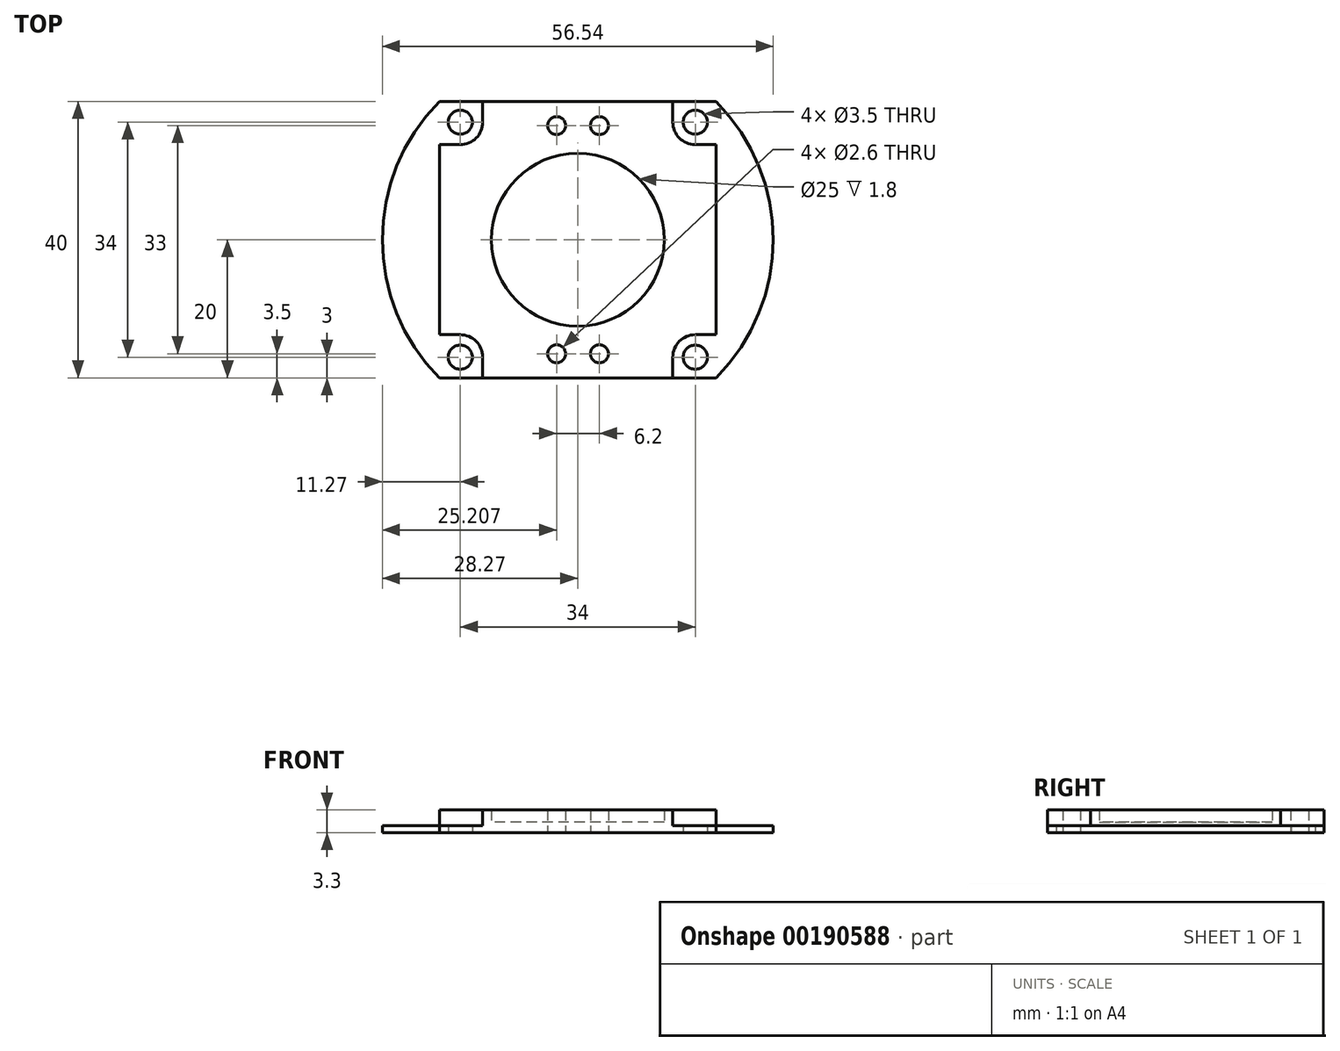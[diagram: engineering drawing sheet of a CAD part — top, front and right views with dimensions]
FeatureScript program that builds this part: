
annotation { "Feature Type Name" : "Feature", "Feature Type Description" : "" }
export const myFeature = defineFeature(function(context is Context, id is Id, definition is map)
    precondition{}
    {
        {
            var Q0;
            Q0=qCreatedBy(makeId("Top.planeOp"),FACE);
            var sketch = newSketch(context, id + "F0", { "sketchPlane" : qUnion([Q0])});
            skLineSegment(sketch, "E0.bottom", {"start": v(20, -20) * mm, "end": v(-20, -20) * mm});
            skLineSegment(sketch, "E0.top", {"start": v(20, 20) * mm, "end": v(-20, 20) * mm});
            skLineSegment(sketch, "E0.left", {"start": v(20, -20) * mm, "end": v(20, 20) * mm});
            skLineSegment(sketch, "E0.right", {"start": v(-20, -20) * mm, "end": v(-20, 20) * mm});
            skPoint(sketch, "E0.middle", {"position": v(0, 0) * mm});
            skArc(sketch, "E1", {"start": v(-20, 20) * mm, "mid": v(-28.27, 0) * mm, "end": v(-20, -20) * mm});
            skArc(sketch, "E2", {"start": v(20, -20) * mm, "mid": v(28.27, 0) * mm, "end": v(20, 20) * mm});
            skLineSegment(sketch, "E3.bottom", {"start": v(13.75, -13.75) * mm, "end": v(-13.75, -13.75) * mm, "construction": true});
            skLineSegment(sketch, "E3.top", {"start": v(13.75, 13.75) * mm, "end": v(-13.75, 13.75) * mm, "construction": true});
            skLineSegment(sketch, "E3.left", {"start": v(13.75, -13.75) * mm, "end": v(13.75, 13.75) * mm, "construction": true});
            skLineSegment(sketch, "E3.right", {"start": v(-13.75, -13.75) * mm, "end": v(-13.75, 13.75) * mm, "construction": true});
            skLineSegment(sketch, "E4", {"start": v(-13.75, 17) * mm, "end": v(-13.75, 20) * mm});
            skLineSegment(sketch, "E5", {"start": v(-17, 13.75) * mm, "end": v(-20, 13.75) * mm});
            skLineSegment(sketch, "E6", {"start": v(13.75, 17) * mm, "end": v(13.75, 20) * mm});
            skLineSegment(sketch, "E7", {"start": v(17, 13.75) * mm, "end": v(20, 13.75) * mm});
            skLineSegment(sketch, "E8", {"start": v(17, -13.75) * mm, "end": v(20, -13.75) * mm});
            skLineSegment(sketch, "E9", {"start": v(13.75, -17) * mm, "end": v(13.75, -20) * mm});
            skLineSegment(sketch, "E10", {"start": v(-13.75, -20) * mm, "end": v(-13.75, -17) * mm});
            skPoint(sketch, "E11.visualSharp", {"position": v(-13.75, 13.75) * mm});
            skArc(sketch, "E11.filletArc", {"start": v(-17, 13.75) * mm, "mid": v(-14.7, 14.7) * mm, "end": v(-13.75, 17) * mm});
            skPoint(sketch, "E12.visualSharp", {"position": v(13.75, 13.75) * mm});
            skArc(sketch, "E12.filletArc", {"start": v(13.75, 17) * mm, "mid": v(14.7, 14.7) * mm, "end": v(17, 13.75) * mm});
            skPoint(sketch, "E13.visualSharp", {"position": v(13.75, -13.75) * mm});
            skArc(sketch, "E13.filletArc", {"start": v(17, -13.75) * mm, "mid": v(14.7, -14.7) * mm, "end": v(13.75, -17) * mm});
            skLineSegment(sketch, "E14", {"start": v(-17, -13.75) * mm, "end": v(-20, -13.75) * mm});
            skPoint(sketch, "E15.visualSharp", {"position": v(-13.75, -13.75) * mm});
            skArc(sketch, "E15.filletArc", {"start": v(-13.75, -17) * mm, "mid": v(-14.7, -14.7) * mm, "end": v(-17, -13.75) * mm});
            skLineSegment(sketch, "E16", {"start": v(0.04, 24.78) * mm, "end": v(0.04, -24.04) * mm, "construction": true});
            skLineSegment(sketch, "E17", {"start": v(-35.36, 0) * mm, "end": v(34.45, 0) * mm, "construction": true});
            skPoint(sketch, "E18", {"position": v(-3.06, 16.5) * mm});
            skPoint(sketch, "E19", {"position": v(3.14, 16.5) * mm});
            skPoint(sketch, "E20", {"position": v(-3.06, -16.5) * mm});
            skPoint(sketch, "E21", {"position": v(3.14, -16.5) * mm});
            skCircle(sketch, "E22", {"center": v(0, 0) * mm, "radius": 12.5 * mm});
            skSolve(sketch);
        }
        {
            var Q0;
            {var subQ8=sQuery(id+"F0.wireOp",EDGE,"E4");Q0=makeQuery(id+"F0.imprint","IMPRINT",FACE,{"disambiguationData":[TD([[makeQuery(id+"F0.imprint","IMPRINT",EDGE,{"derivedFrom":subQ8}),-1.0]])]});}
            extrude(context, id + "F1", {"entities" : qUnion([Q0]), "depth" : 3.3 * mm});
        }
        {
            var Q0;
            Q0=makeQuery(id+"F0.imprint","IMPRINT",FACE,{"disambiguationData":[TD([[makeQuery(id+"F0.imprint","IMPRINT",EDGE,{"derivedFrom":sQuery(id+"F0.wireOp",EDGE,"E22")}),1.0]])]});
            extrude(context, id + "F2", {"entities" : qUnion([Q0]), "operationType" : NewBodyOperationType.ADD, "depth" : 1.5 * mm});
        }
        {
            var Q0;
            {var subQ0=sQuery(id+"F0.wireOp",EDGE,"E2");Q0=makeQuery(id+"F0.imprint","IMPRINT",FACE,{"disambiguationData":[TD([[makeQuery(id+"F0.imprint","IMPRINT",EDGE,{"derivedFrom":subQ0}),1.0]])]});}
            var Q1;
            {var subQ4=sQuery(id+"F0.wireOp",EDGE,"E6");Q1=makeQuery(id+"F0.imprint","IMPRINT",FACE,{"disambiguationData":[TD([[makeQuery(id+"F0.imprint","IMPRINT",EDGE,{"derivedFrom":subQ4}),-1.0]])]});}
            var Q2;
            {var subQ4=sQuery(id+"F0.wireOp",EDGE,"E8");Q2=makeQuery(id+"F0.imprint","IMPRINT",FACE,{"disambiguationData":[TD([[makeQuery(id+"F0.imprint","IMPRINT",EDGE,{"derivedFrom":subQ4}),-1.0]])]});}
            var Q3;
            {var subQ1=sQuery(id+"F0.wireOp",EDGE,"E4");Q3=makeQuery(id+"F0.imprint","IMPRINT",FACE,{"disambiguationData":[TD([[makeQuery(id+"F0.imprint","IMPRINT",EDGE,{"derivedFrom":subQ1}),1.0]])]});}
            var Q4;
            {var subQ0=sQuery(id+"F0.wireOp",EDGE,"E1");Q4=makeQuery(id+"F0.imprint","IMPRINT",FACE,{"disambiguationData":[TD([[makeQuery(id+"F0.imprint","IMPRINT",EDGE,{"derivedFrom":subQ0}),1.0]])]});}
            var Q5;
            {var subQ0=sQuery(id+"F0.wireOp",EDGE,"E10");Q5=makeQuery(id+"F0.imprint","IMPRINT",FACE,{"disambiguationData":[TD([[makeQuery(id+"F0.imprint","IMPRINT",EDGE,{"derivedFrom":subQ0}),1.0]])]});}
            extrude(context, id + "F3", {"entities" : qUnion([Q0, Q1, Q2, Q3, Q4, Q5]), "operationType" : NewBodyOperationType.ADD, "depth" : 1 * mm});
        }
        {
            var Q0;
            Q0=sQuery(id+"F0.wireOp",VERTEX,"E12.filletArc.center");
            var Q1;
            Q1=sQuery(id+"F0.wireOp",VERTEX,"E11.filletArc.center");
            var Q2;
            Q2=sQuery(id+"F0.wireOp",VERTEX,"E15.filletArc.center");
            var Q3;
            Q3=sQuery(id+"F0.wireOp",VERTEX,"E13.filletArc.center");
            var Q4;
            Q4=makeQuery(id+"F1.opExtrude","SWEPT_BODY",BODY,{"disambiguationData":[OSD([sQuery(id+"F0.wireOp",EDGE,"E0.bottom"),sQuery(id+"F0.wireOp",EDGE,"E0.top"),sQuery(id+"F0.wireOp",EDGE,"E0.left"),sQuery(id+"F0.wireOp",EDGE,"E0.right"),sQuery(id+"F0.wireOp",EDGE,"E4"),sQuery(id+"F0.wireOp",EDGE,"E5"),sQuery(id+"F0.wireOp",EDGE,"E6"),sQuery(id+"F0.wireOp",EDGE,"E7"),sQuery(id+"F0.wireOp",EDGE,"E8"),sQuery(id+"F0.wireOp",EDGE,"E9"),sQuery(id+"F0.wireOp",EDGE,"E10"),sQuery(id+"F0.wireOp",EDGE,"E11.filletArc"),sQuery(id+"F0.wireOp",EDGE,"E12.filletArc"),sQuery(id+"F0.wireOp",EDGE,"E13.filletArc"),sQuery(id+"F0.wireOp",EDGE,"E14"),sQuery(id+"F0.wireOp",EDGE,"E15.filletArc"),sQuery(id+"F0.wireOp",EDGE,"E22")])]});
            hole(context, id + "F4", {"style" : HoleStyle.SIMPLE, "endStyle" : HoleEndStyle.THROUGH, "oppositeDirection" : true, "holeDiameter" : 3.5 * mm, "locations" : qUnion([Q0, Q1, Q2, Q3]), "scope" : qUnion([Q4]), "isTappedThrough" : true});
        }
        {
            var Q0;
            Q0=sQuery(id+"F0.wireOp",VERTEX,"E18");
            var Q1;
            Q1=sQuery(id+"F0.wireOp",VERTEX,"E19");
            var Q2;
            Q2=sQuery(id+"F0.wireOp",VERTEX,"E21");
            var Q3;
            Q3=sQuery(id+"F0.wireOp",VERTEX,"E20");
            var Q4;
            Q4=makeQuery(id+"F1.opExtrude","SWEPT_BODY",BODY,{"disambiguationData":[OSD([sQuery(id+"F0.wireOp",EDGE,"E0.bottom"),sQuery(id+"F0.wireOp",EDGE,"E0.top"),sQuery(id+"F0.wireOp",EDGE,"E0.left"),sQuery(id+"F0.wireOp",EDGE,"E0.right"),sQuery(id+"F0.wireOp",EDGE,"E4"),sQuery(id+"F0.wireOp",EDGE,"E5"),sQuery(id+"F0.wireOp",EDGE,"E6"),sQuery(id+"F0.wireOp",EDGE,"E7"),sQuery(id+"F0.wireOp",EDGE,"E8"),sQuery(id+"F0.wireOp",EDGE,"E9"),sQuery(id+"F0.wireOp",EDGE,"E10"),sQuery(id+"F0.wireOp",EDGE,"E11.filletArc"),sQuery(id+"F0.wireOp",EDGE,"E12.filletArc"),sQuery(id+"F0.wireOp",EDGE,"E13.filletArc"),sQuery(id+"F0.wireOp",EDGE,"E14"),sQuery(id+"F0.wireOp",EDGE,"E15.filletArc"),sQuery(id+"F0.wireOp",EDGE,"E22")])]});
            hole(context, id + "F5", {"style" : HoleStyle.SIMPLE, "endStyle" : HoleEndStyle.THROUGH, "oppositeDirection" : true, "holeDiameter" : 2.6 * mm, "locations" : qUnion([Q0, Q1, Q2, Q3]), "scope" : qUnion([Q4]), "isTappedThrough" : true});
        }
    });
